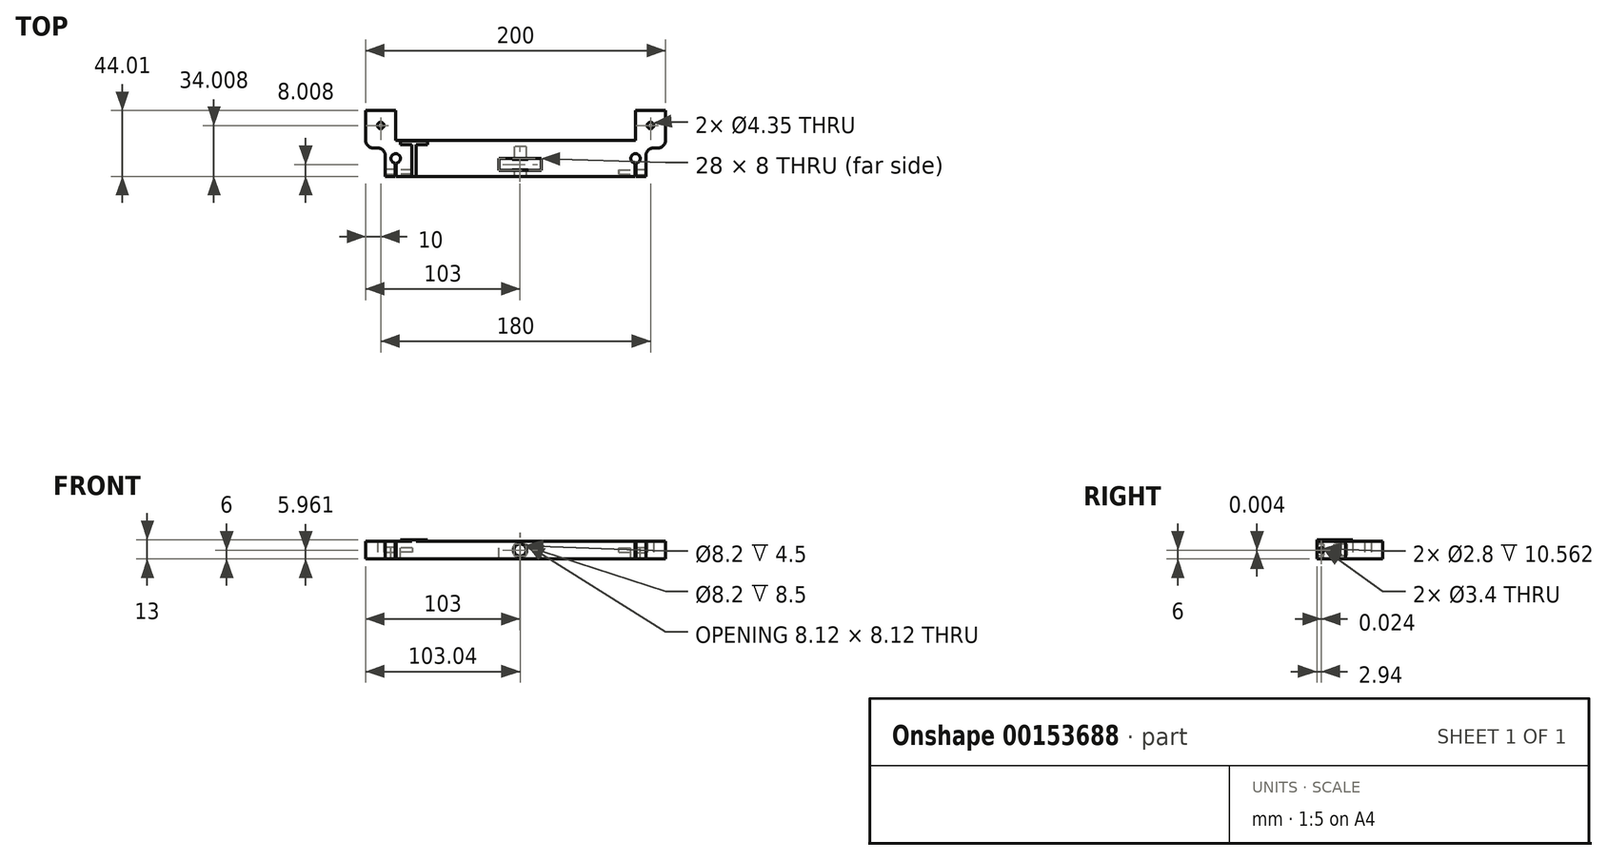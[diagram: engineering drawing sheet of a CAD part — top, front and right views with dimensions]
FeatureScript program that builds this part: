
annotation { "Feature Type Name" : "Feature", "Feature Type Description" : "" }
export const myFeature = defineFeature(function(context is Context, id is Id, definition is map)
    precondition{}
    {
        {
            var Q0;
            Q0=qCreatedBy(makeId("Top.planeOp"),FACE);
            var sketch = newSketch(context, id + "F0", { "sketchPlane" : qUnion([Q0])});
            skLineSegment(sketch, "E0", {"start": v(-46.35, 12.3) * mm, "end": v(153.65, 12.3) * mm});
            skLineSegment(sketch, "E1", {"start": v(153.65, 12.3) * mm, "end": v(153.65, 7.3) * mm});
            skLineSegment(sketch, "E2", {"start": v(153.65, 7.3) * mm, "end": v(140.65, 7.3) * mm});
            skLineSegment(sketch, "E3", {"start": v(140.65, 7.3) * mm, "end": v(140.65, -11.7) * mm});
            skLineSegment(sketch, "E4", {"start": v(140.65, -11.7) * mm, "end": v(-33.35, -11.7) * mm});
            skLineSegment(sketch, "E5", {"start": v(-33.35, -11.7) * mm, "end": v(-33.35, 7.3) * mm});
            skLineSegment(sketch, "E6", {"start": v(-33.35, 7.3) * mm, "end": v(-46.35, 7.3) * mm});
            skLineSegment(sketch, "E7", {"start": v(-46.35, 7.3) * mm, "end": v(-46.35, 12.3) * mm});
            skSolve(sketch);
        }
        {
            var Q0;
            Q0=qSketchRegion(id+"F0",true);
            extrude(context, id + "F1", {"entities" : qUnion([Q0]), "depth" : 12 * mm});
        }
        {
            var Q0;
            Q0=makeQuery(id+"F1.opExtrude","CAP_FACE",FACE,{"disambiguationData":[OSD([sQuery(id+"F0.wireOp",EDGE,"E0"),sQuery(id+"F0.wireOp",EDGE,"E1"),sQuery(id+"F0.wireOp",EDGE,"E2"),sQuery(id+"F0.wireOp",EDGE,"E3"),sQuery(id+"F0.wireOp",EDGE,"E4"),sQuery(id+"F0.wireOp",EDGE,"E5"),sQuery(id+"F0.wireOp",EDGE,"E6"),sQuery(id+"F0.wireOp",EDGE,"E7")])],"isStart":false});
            var sketch = newSketch(context, id + "F2", { "sketchPlane" : qUnion([Q0])});
            skCircle(sketch, "E8", {"center": v(-26.35, 0.3) * mm, "radius": 3.15 * mm});
            skCircle(sketch, "E9", {"center": v(133.65, 0.3) * mm, "radius": 3.15 * mm});
            skPoint(sketch, "E10", {"position": v(53.65, 12.3) * mm});
            skLineSegment(sketch, "E11.bottom", {"start": v(133.21, -2.43) * mm, "end": v(134.09, -2.43) * mm});
            skLineSegment(sketch, "E11.top", {"start": v(133.21, -11.7) * mm, "end": v(134.09, -11.7) * mm});
            skLineSegment(sketch, "E11.left", {"start": v(133.21, -2.43) * mm, "end": v(133.21, -11.7) * mm});
            skLineSegment(sketch, "E11.right", {"start": v(134.09, -2.43) * mm, "end": v(134.09, -11.7) * mm});
            skPoint(sketch, "E12", {"position": v(133.65, -2.43) * mm});
            skLineSegment(sketch, "E13", {"start": v(53.65, 12.3) * mm, "end": v(53.65, -11.7) * mm, "construction": true});
            skLineSegment(sketch, "E14.MirrorCS", {"start": v(-25.91, -11.7) * mm, "end": v(-26.79, -11.7) * mm});
            skLineSegment(sketch, "E15.MirrorCS", {"start": v(-26.79, -2.43) * mm, "end": v(-26.79, -11.7) * mm});
            skLineSegment(sketch, "E16.MirrorCS", {"start": v(-25.91, -2.43) * mm, "end": v(-26.79, -2.43) * mm});
            skLineSegment(sketch, "E17.MirrorCS", {"start": v(-25.91, -2.43) * mm, "end": v(-25.91, -11.7) * mm});
            skSolve(sketch);
        }
        {
            var Q0;
            Q0=qSketchRegion(id+"F2",true);
            var Q1;
            {var subQ3=sQuery(id+"F2.wireOp",EDGE,"E11.bottom");Q1=makeQuery(id+"F2.imprint","IMPRINT",FACE,{"disambiguationData":[TD([[makeQuery(id+"F2.imprint","IMPRINT",EDGE,{"derivedFrom":subQ3}),-1.0]])]});}
            var Q2;
            {var subQ3=sQuery(id+"F2.wireOp",EDGE,"E16.MirrorCS");Q2=makeQuery(id+"F2.imprint","IMPRINT",FACE,{"disambiguationData":[TD([[makeQuery(id+"F2.imprint","IMPRINT",EDGE,{"derivedFrom":subQ3}),1.0]])]});}
            extrude(context, id + "F3", {"entities" : qUnion([Q0, Q1, Q2]), "operationType" : NewBodyOperationType.REMOVE, "endBound" : BoundingType.THROUGH_ALL, "oppositeDirection" : true, "depth" : 25 * mm});
        }
        {
            var Q0;
            Q0=makeQuery(id+"F1.opExtrude","SWEPT_FACE",FACE,{"disambiguationData":[OSD([sQuery(id+"F0.wireOp",EDGE,"E4")])]});
            var sketch = newSketch(context, id + "F4", { "sketchPlane" : qUnion([Q0])});
            skLineSegment(sketch, "E18", {"start": v(-33.35, 6) * mm, "end": v(140.65, 6) * mm, "construction": true});
            skCircle(sketch, "E19", {"center": v(56.65, 6) * mm, "radius": 4.1 * mm});
            skSolve(sketch);
        }
        {
            var Q0;
            Q0=qSketchRegion(id+"F4",true);
            extrude(context, id + "F5", {"entities" : qUnion([Q0]), "operationType" : NewBodyOperationType.REMOVE, "oppositeDirection" : true, "depth" : 20 * mm});
        }
        {
            var Q0;
            Q0=makeQuery(id+"F1.opExtrude","CAP_FACE",FACE,{"disambiguationData":[OSD([sQuery(id+"F0.wireOp",EDGE,"E0"),sQuery(id+"F0.wireOp",EDGE,"E1"),sQuery(id+"F0.wireOp",EDGE,"E2"),sQuery(id+"F0.wireOp",EDGE,"E3"),sQuery(id+"F0.wireOp",EDGE,"E4"),sQuery(id+"F0.wireOp",EDGE,"E5"),sQuery(id+"F0.wireOp",EDGE,"E6"),sQuery(id+"F0.wireOp",EDGE,"E7")])],"isStart":false});
            var sketch = newSketch(context, id + "F6", { "sketchPlane" : qUnion([Q0])});
            skLineSegment(sketch, "E20.bottom", {"start": v(42.65, 0.3) * mm, "end": v(70.65, 0.3) * mm});
            skLineSegment(sketch, "E20.top", {"start": v(42.65, -7.7) * mm, "end": v(70.65, -7.7) * mm});
            skLineSegment(sketch, "E20.left", {"start": v(42.65, 0.3) * mm, "end": v(42.65, -7.7) * mm});
            skLineSegment(sketch, "E20.right", {"start": v(70.65, 0.3) * mm, "end": v(70.65, -7.7) * mm});
            skLineSegment(sketch, "E21", {"start": v(56.65, 12.3) * mm, "end": v(56.65, -11.7) * mm, "construction": true});
            skLineSegment(sketch, "E22", {"start": v(56.65, 0.3) * mm, "end": v(56.65, -7.7) * mm});
            skSolve(sketch);
        }
        {
            var Q0;
            Q0=qSketchRegion(id+"F6",true);
            extrude(context, id + "F7", {"entities" : qUnion([Q0]), "operationType" : NewBodyOperationType.REMOVE, "endBound" : BoundingType.THROUGH_ALL, "oppositeDirection" : true, "depth" : 25 * mm});
        }
        {
            var Q0;
            Q0=makeQuery(id+"F7.boolean.opBoolean","COPY",FACE,{"derivedFrom":makeQuery(id+"F7.opExtrude","SWEPT_FACE",FACE,{"disambiguationData":[OSD([sQuery(id+"F6.wireOp",EDGE,"E20.bottom")])]})});
            var sketch = newSketch(context, id + "F8", { "sketchPlane" : qUnion([Q0])});
            skCircle(sketch, "E23", {"center": v(56.65, 6) * mm, "radius": 5.2 * mm});
            skSolve(sketch);
        }
        {
            var Q0;
            Q0=makeQuery(id+"F8.imprint","IMPRINT",FACE,{"disambiguationData":[TD([[makeQuery(id+"F8.imprint","IMPRINT",EDGE,{"derivedFrom":sQuery(id+"F8.wireOp",EDGE,"E23")}),1.0]])]});
            extrude(context, id + "F9", {"entities" : qUnion([Q0]), "operationType" : NewBodyOperationType.ADD, "depth" : 0.5 * mm});
        }
        {
            var Q0;
            Q0=makeQuery(id+"F7.boolean.opBoolean","COPY",FACE,{"derivedFrom":makeQuery(id+"F7.opExtrude","SWEPT_FACE",FACE,{"disambiguationData":[OSD([sQuery(id+"F6.wireOp",EDGE,"E20.top")])]})});
            var sketch = newSketch(context, id + "F10", { "sketchPlane" : qUnion([Q0])});
            skCircle(sketch, "E24", {"center": v(-56.65, 6) * mm, "radius": 5.25 * mm});
            skSolve(sketch);
        }
        {
            var Q0;
            Q0=makeQuery(id+"F10.imprint","IMPRINT",FACE,{"disambiguationData":[TD([[makeQuery(id+"F10.imprint","IMPRINT",EDGE,{"derivedFrom":sQuery(id+"F10.wireOp",EDGE,"E24")}),1.0]])]});
            extrude(context, id + "F11", {"entities" : qUnion([Q0]), "operationType" : NewBodyOperationType.ADD, "depth" : 0.5 * mm});
        }
        {
            var Q0;
            Q0=makeQuery(id+"F1.opExtrude","CAP_FACE",FACE,{"disambiguationData":[OSD([sQuery(id+"F0.wireOp",EDGE,"E0"),sQuery(id+"F0.wireOp",EDGE,"E1"),sQuery(id+"F0.wireOp",EDGE,"E2"),sQuery(id+"F0.wireOp",EDGE,"E3"),sQuery(id+"F0.wireOp",EDGE,"E4"),sQuery(id+"F0.wireOp",EDGE,"E5"),sQuery(id+"F0.wireOp",EDGE,"E6"),sQuery(id+"F0.wireOp",EDGE,"E7")])],"isStart":false});
            var sketch = newSketch(context, id + "F12", { "sketchPlane" : qUnion([Q0])});
            skText(sketch, "E25", { "text": "T", "fontName": "OpenSans-Regular.ttf"});
            const initialGuessF12  = {"E25": [-0.02337, -0.0117, 1, 0, 0.024]};
            skSetInitialGuess(sketch, initialGuessF12);
            skSolve(sketch);
        }
        {
            var Q0;
            Q0=qSketchRegion(id+"F12",true);
            extrude(context, id + "F13", {"entities" : qUnion([Q0]), "operationType" : NewBodyOperationType.ADD, "depth" : 1 * mm});
        }
        {
            var Q0;
            Q0=makeQuery(id+"F1.opExtrude","SWEPT_FACE",FACE,{"disambiguationData":[OSD([sQuery(id+"F0.wireOp",EDGE,"E3")])]});
            var sketch = newSketch(context, id + "F14", { "sketchPlane" : qUnion([Q0])});
            skCircle(sketch, "E26", {"center": v(-8.74, 6) * mm, "radius": 1.7 * mm});
            skCircle(sketch, "E27", {"center": v(-8.74, 6) * mm, "radius": 1.4 * mm});
            skLineSegment(sketch, "E28", {"start": v(-11.7, 6) * mm, "end": v(-3.84, 6) * mm, "construction": true});
            skSolve(sketch);
        }
        {
            var Q0;
            Q0=makeQuery(id+"F14.imprint","IMPRINT",FACE,{"disambiguationData":[TD([[makeQuery(id+"F14.imprint","IMPRINT",EDGE,{"derivedFrom":sQuery(id+"F14.wireOp",EDGE,"E27")}),1.0]])]});
            extrude(context, id + "F15", {"entities" : qUnion([Q0]), "operationType" : NewBodyOperationType.REMOVE, "oppositeDirection" : true, "depth" : 18 * mm});
        }
        {
            var Q0;
            Q0=makeQuery(id+"F14.imprint","IMPRINT",FACE,{"disambiguationData":[TD([[makeQuery(id+"F14.imprint","IMPRINT",EDGE,{"derivedFrom":sQuery(id+"F14.wireOp",EDGE,"E27")}),1.0]])]});
            var Q1;
            Q1=makeQuery(id+"F14.imprint","IMPRINT",FACE,{"disambiguationData":[TD([[makeQuery(id+"F14.imprint","IMPRINT",EDGE,{"derivedFrom":sQuery(id+"F14.wireOp",EDGE,"E26")}),1.0]])]});
            extrude(context, id + "F16", {"entities" : qUnion([Q0, Q1]), "operationType" : NewBodyOperationType.REMOVE, "endBound" : BoundingType.UP_TO_NEXT, "oppositeDirection" : true, "depth" : 7 * mm});
        }
        {
            var Q0;
            Q0=makeQuery(id+"F1.opExtrude","SWEPT_EDGE",EDGE,{"disambiguationData":[OSD([sQuery(id+"F0.wireOp",EDGE,"E2"),sQuery(id+"F0.wireOp",EDGE,"E3")])]});
            fillet(context, id + "F17", {"entities" : qUnion([Q0]), "radius" : 5 * mm, "tangentPropagation" : true, "allowEdgeOverflow" : false});
        }
        {
            var Q0;
            Q0=makeQuery(id+"F1.opExtrude","SWEPT_FACE",FACE,{"disambiguationData":[OSD([sQuery(id+"F0.wireOp",EDGE,"E5")])]});
            var sketch = newSketch(context, id + "F18", { "sketchPlane" : qUnion([Q0])});
            skCircle(sketch, "E29", {"center": v(8.76, 6) * mm, "radius": 1.7 * mm});
            skCircle(sketch, "E30", {"center": v(8.76, 6) * mm, "radius": 1.4 * mm});
            skLineSegment(sketch, "E31", {"start": v(8.76, 0) * mm, "end": v(8.76, 12) * mm, "construction": true});
            skSolve(sketch);
        }
        {
            var Q0;
            Q0=makeQuery(id+"F18.imprint","IMPRINT",FACE,{"disambiguationData":[TD([[makeQuery(id+"F18.imprint","IMPRINT",EDGE,{"derivedFrom":sQuery(id+"F18.wireOp",EDGE,"E30")}),1.0]])]});
            extrude(context, id + "F19", {"entities" : qUnion([Q0]), "operationType" : NewBodyOperationType.REMOVE, "oppositeDirection" : true, "depth" : 18 * mm});
        }
        {
            var Q0;
            Q0=makeQuery(id+"F18.imprint","IMPRINT",FACE,{"disambiguationData":[TD([[makeQuery(id+"F18.imprint","IMPRINT",EDGE,{"derivedFrom":sQuery(id+"F18.wireOp",EDGE,"E30")}),1.0]])]});
            var Q1;
            Q1=makeQuery(id+"F18.imprint","IMPRINT",FACE,{"disambiguationData":[TD([[makeQuery(id+"F18.imprint","IMPRINT",EDGE,{"derivedFrom":sQuery(id+"F18.wireOp",EDGE,"E29")}),1.0]])]});
            extrude(context, id + "F20", {"entities" : qUnion([Q0, Q1]), "operationType" : NewBodyOperationType.REMOVE, "endBound" : BoundingType.UP_TO_NEXT, "oppositeDirection" : true, "depth" : 25 * mm});
        }
        {
            var Q0;
            Q0=makeQuery(id+"F1.opExtrude","SWEPT_EDGE",EDGE,{"disambiguationData":[OSD([sQuery(id+"F0.wireOp",EDGE,"E5"),sQuery(id+"F0.wireOp",EDGE,"E6")])]});
            fillet(context, id + "F21", {"entities" : qUnion([Q0]), "radius" : 5 * mm, "tangentPropagation" : true, "allowEdgeOverflow" : false});
        }
        {
            var Q0;
            Q0=makeQuery(id+"F1.opExtrude","SWEPT_FACE",FACE,{"disambiguationData":[OSD([sQuery(id+"F0.wireOp",EDGE,"E0")])]});
            var sketch = newSketch(context, id + "F22", { "sketchPlane" : qUnion([Q0])});
            skLineSegment(sketch, "E32.bottom", {"start": v(-153.65, 12) * mm, "end": v(-133.65, 12) * mm});
            skLineSegment(sketch, "E32.top", {"start": v(-153.65, 0) * mm, "end": v(-133.65, 0) * mm});
            skLineSegment(sketch, "E32.left", {"start": v(-153.65, 12) * mm, "end": v(-153.65, 0) * mm});
            skLineSegment(sketch, "E32.right", {"start": v(-133.65, 12) * mm, "end": v(-133.65, 0) * mm});
            skLineSegment(sketch, "E33.bottom", {"start": v(46.35, 12) * mm, "end": v(26.35, 12) * mm});
            skLineSegment(sketch, "E33.top", {"start": v(46.35, 0) * mm, "end": v(26.35, 0) * mm});
            skLineSegment(sketch, "E33.left", {"start": v(46.35, 12) * mm, "end": v(46.35, 0) * mm});
            skLineSegment(sketch, "E33.right", {"start": v(26.35, 12) * mm, "end": v(26.35, 0) * mm});
            skSolve(sketch);
        }
        {
            var Q0;
            Q0=qSketchRegion(id+"F22",true);
            extrude(context, id + "F23", {"entities" : qUnion([Q0]), "operationType" : NewBodyOperationType.ADD, "depth" : 20 * mm});
        }
        {
            var Q0;
            Q0=makeQuery(id+"F1.opExtrude","SWEPT_EDGE",EDGE,{"disambiguationData":[OSD([sQuery(id+"F0.wireOp",EDGE,"E1"),sQuery(id+"F0.wireOp",EDGE,"E2")])]});
            var Q1;
            Q1=makeQuery(id+"F1.opExtrude","SWEPT_EDGE",EDGE,{"disambiguationData":[OSD([sQuery(id+"F0.wireOp",EDGE,"E6"),sQuery(id+"F0.wireOp",EDGE,"E7")])]});
            fillet(context, id + "F24", {"entities" : qUnion([Q0, Q1]), "radius" : 5 * mm, "tangentPropagation" : true, "allowEdgeOverflow" : false});
        }
        {
            var Q0;
            Q0=makeQuery(id+"F23.boolean.opBoolean","MERGE",FACE,{"derivedFrom":[makeQuery(id+"F1.opExtrude","CAP_FACE",FACE,{"disambiguationData":[OSD([sQuery(id+"F0.wireOp",EDGE,"E0"),sQuery(id+"F0.wireOp",EDGE,"E1"),sQuery(id+"F0.wireOp",EDGE,"E2"),sQuery(id+"F0.wireOp",EDGE,"E3"),sQuery(id+"F0.wireOp",EDGE,"E4"),sQuery(id+"F0.wireOp",EDGE,"E5"),sQuery(id+"F0.wireOp",EDGE,"E6"),sQuery(id+"F0.wireOp",EDGE,"E7")])],"isStart":false}),makeQuery(id+"F23.opExtrude","SWEPT_FACE",FACE,{"disambiguationData":[OSD([sQuery(id+"F22.wireOp",EDGE,"E32.bottom")])]}),makeQuery(id+"F23.opExtrude","SWEPT_FACE",FACE,{"disambiguationData":[OSD([sQuery(id+"F22.wireOp",EDGE,"E33.bottom")])]})]});
            var sketch = newSketch(context, id + "F25", { "sketchPlane" : qUnion([Q0])});
            skLineSegment(sketch, "E34.bottom", {"start": v(-46.35, 32.3) * mm, "end": v(-26.35, 32.3) * mm});
            skLineSegment(sketch, "E34.top", {"start": v(-46.35, 12.3) * mm, "end": v(-26.35, 12.3) * mm});
            skLineSegment(sketch, "E34.left", {"start": v(-46.35, 32.3) * mm, "end": v(-46.35, 12.3) * mm});
            skLineSegment(sketch, "E34.right", {"start": v(-26.35, 32.3) * mm, "end": v(-26.35, 12.3) * mm});
            skLineSegment(sketch, "E35.bottom", {"start": v(153.65, 32.3) * mm, "end": v(133.65, 32.3) * mm});
            skLineSegment(sketch, "E35.top", {"start": v(153.65, 12.3) * mm, "end": v(133.65, 12.3) * mm});
            skLineSegment(sketch, "E35.left", {"start": v(153.65, 32.3) * mm, "end": v(153.65, 12.3) * mm});
            skLineSegment(sketch, "E35.right", {"start": v(133.65, 32.3) * mm, "end": v(133.65, 12.3) * mm});
            skSolve(sketch);
        }
        {
            var Q0;
            Q0=makeQuery(id+"F23.boolean.opBoolean","MERGE",FACE,{"derivedFrom":[makeQuery(id+"F1.opExtrude","CAP_FACE",FACE,{"disambiguationData":[OSD([sQuery(id+"F0.wireOp",EDGE,"E0"),sQuery(id+"F0.wireOp",EDGE,"E1"),sQuery(id+"F0.wireOp",EDGE,"E2"),sQuery(id+"F0.wireOp",EDGE,"E3"),sQuery(id+"F0.wireOp",EDGE,"E4"),sQuery(id+"F0.wireOp",EDGE,"E5"),sQuery(id+"F0.wireOp",EDGE,"E6"),sQuery(id+"F0.wireOp",EDGE,"E7")])],"isStart":true}),makeQuery(id+"F23.opExtrude","SWEPT_FACE",FACE,{"disambiguationData":[OSD([sQuery(id+"F22.wireOp",EDGE,"E32.top")])]}),makeQuery(id+"F23.opExtrude","SWEPT_FACE",FACE,{"disambiguationData":[OSD([sQuery(id+"F22.wireOp",EDGE,"E33.top")])]})]});
            var sketch = newSketch(context, id + "F26", { "sketchPlane" : qUnion([Q0])});
            skCircle(sketch, "E36", {"center": v(-36.35, -22.3) * mm, "radius": 2.17 * mm});
            skCircle(sketch, "E37", {"center": v(143.65, -22.3) * mm, "radius": 2.17 * mm});
            skPoint(sketch, "E38", {"position": v(-36.35, -32.3) * mm});
            skPoint(sketch, "E39", {"position": v(143.65, -32.3) * mm});
            skSolve(sketch);
        }
        {
            var Q0;
            Q0=makeQuery(id+"F26.imprint","IMPRINT",FACE,{"disambiguationData":[TD([[makeQuery(id+"F26.imprint","IMPRINT",EDGE,{"derivedFrom":sQuery(id+"F26.wireOp",EDGE,"E36")}),1.0]])]});
            var Q1;
            Q1=makeQuery(id+"F26.imprint","IMPRINT",FACE,{"disambiguationData":[TD([[makeQuery(id+"F26.imprint","IMPRINT",EDGE,{"derivedFrom":sQuery(id+"F26.wireOp",EDGE,"E37")}),1.0]])]});
            extrude(context, id + "F27", {"entities" : qUnion([Q0, Q1]), "operationType" : NewBodyOperationType.REMOVE, "endBound" : BoundingType.THROUGH_ALL, "oppositeDirection" : true, "depth" : 25 * mm});
        }
        {
            var Q0;
            Q0=makeQuery(id+"F23.boolean.opBoolean","MERGE",FACE,{"derivedFrom":[makeQuery(id+"F1.opExtrude","CAP_FACE",FACE,{"disambiguationData":[OSD([sQuery(id+"F0.wireOp",EDGE,"E0"),sQuery(id+"F0.wireOp",EDGE,"E1"),sQuery(id+"F0.wireOp",EDGE,"E2"),sQuery(id+"F0.wireOp",EDGE,"E3"),sQuery(id+"F0.wireOp",EDGE,"E4"),sQuery(id+"F0.wireOp",EDGE,"E5"),sQuery(id+"F0.wireOp",EDGE,"E6"),sQuery(id+"F0.wireOp",EDGE,"E7")])],"isStart":false}),makeQuery(id+"F23.opExtrude","SWEPT_FACE",FACE,{"disambiguationData":[OSD([sQuery(id+"F22.wireOp",EDGE,"E32.bottom")])]}),makeQuery(id+"F23.opExtrude","SWEPT_FACE",FACE,{"disambiguationData":[OSD([sQuery(id+"F22.wireOp",EDGE,"E33.bottom")])]})]});
            var sketch = newSketch(context, id + "F28", { "sketchPlane" : qUnion([Q0])});
            skLineSegment(sketch, "E40.0", {"start": v(-36.35, 27.3) * mm, "end": v(143.65, 27.3) * mm});
            skSolve(sketch);
        }
    });
